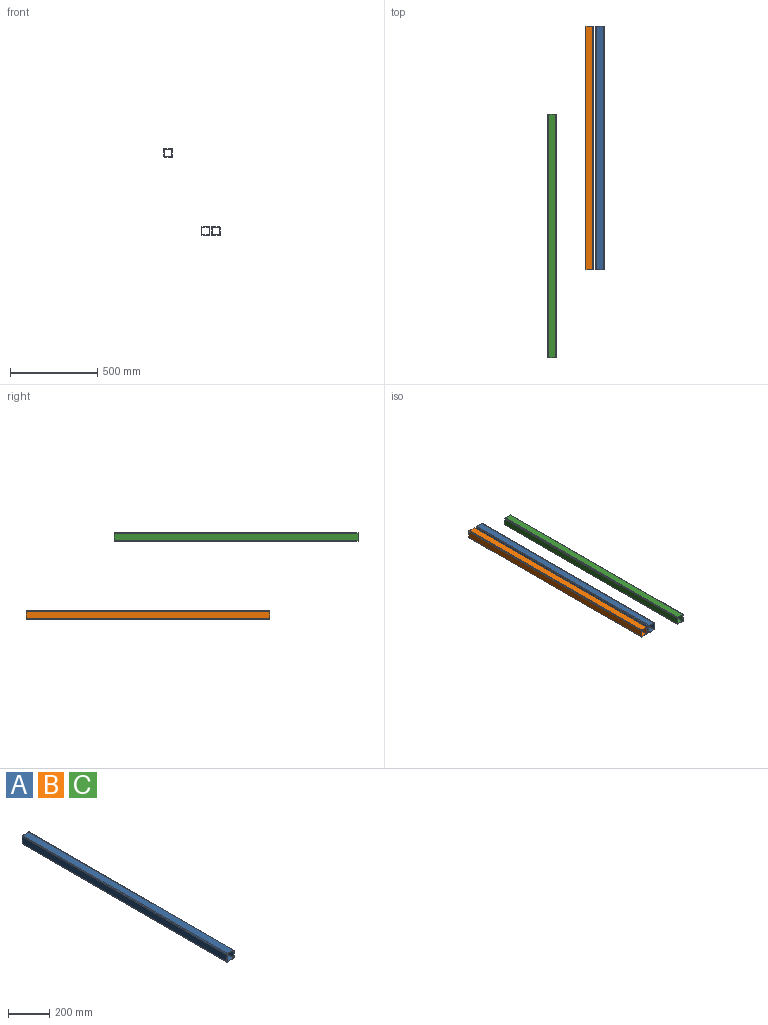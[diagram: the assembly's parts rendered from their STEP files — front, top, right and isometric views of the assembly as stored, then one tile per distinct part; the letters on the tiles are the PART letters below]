
ASSEMBLY  parts=3 mates=1
PART A: 14 faces, bbox 50x1400x50 mm
  f0: plane 1400x40mm, normal (1,0,0), area 56000mm2, adj f1,f11,f12,f13
  f1: cylinder r=5mm len=1400mm, axis (0,-1,0), area 10995.6mm2, adj f0,f2,f12,f13
  f2: plane 1400x40mm, normal (0,0,1), area 56000mm2, adj f1,f3,f12,f13
  f3: cylinder r=5mm len=1400mm, axis (0,-1,0), area 10995.6mm2, adj f2,f4,f12,f13
  f4: plane 1400x40mm, normal (-1,0,0), area 56000mm2, adj f3,f5,f12,f13
  f5: cylinder r=5mm len=1400mm, axis (0,-1,0), area 10995.6mm2, adj f4,f6,f12,f13
  f6: plane 1400x40mm, normal (0,0,-1), area 56000mm2, adj f5,f11,f12,f13
  f7: plane 1400x44mm, normal (1,0,0), area 61600mm2, adj f8,f10,f12,f13
  f8: plane 1400x44mm, normal (0,0,-1), area 61600mm2, adj f7,f9,f12,f13
  f9: plane 1400x44mm, normal (-1,0,0), area 61600mm2, adj f8,f10,f12,f13
  f10: plane 1400x44mm, normal (0,0,1), area 61600mm2, adj f7,f9,f12,f13
  f11: cylinder r=5mm len=1400mm, axis (0,-1,0), area 10995.6mm2, adj f0,f6,f12,f13
  f12: plane 50x50mm, normal (0,1,0), area 542.5mm2, adj f0,f1,f2,f3,f4,f5,f6,f7
  f13: plane 50x50mm, normal (0,-1,0), area 542.5mm2, adj f0,f1,f2,f3,f4,f5,f6,f7
PART B: same geometry as A
PART C: same geometry as A
PLACE A t=(60,0,25)mm
PLACE B t=(0,0,25)mm
PLACE C t=(-214.59,-507.46,474.66)mm
MATE fastened A.f13 <-> B.f13  axis (0,-1,0) through (60,0,25)mm
